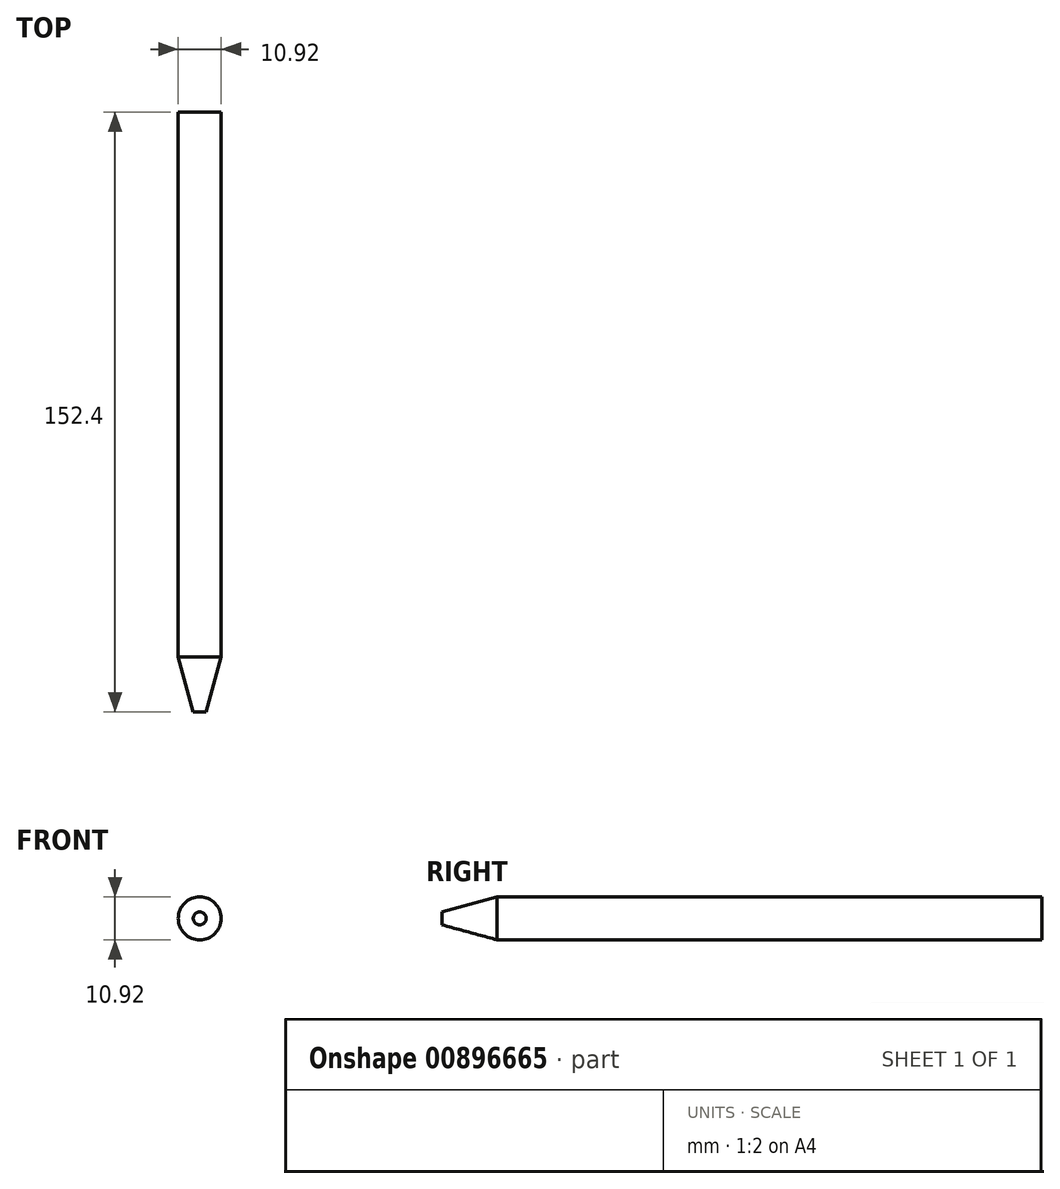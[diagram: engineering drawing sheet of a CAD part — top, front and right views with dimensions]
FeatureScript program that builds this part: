
annotation { "Feature Type Name" : "Feature", "Feature Type Description" : "" }
export const myFeature = defineFeature(function(context is Context, id is Id, definition is map)
    precondition{}
    {
        {
            var Q0;
            Q0=qCreatedBy(makeId("Front.planeOp"),FACE);
            var sketch = newSketch(context, id + "F0", { "sketchPlane" : qUnion([Q0])});
            skCircle(sketch, "E0", {"center": v(0, 0) * mm, "radius": 5.46 * mm});
            skSolve(sketch);
        }
        {
            var Q0;
            Q0 = qSketchRegion(id + "F0", true);
            extrude(context, id + "F1", {"entities" : qUnion([Q0]), "endBound" : BoundingType.SYMMETRIC, "depth" : 152.4 * mm, "offsetDistance" : 25.4 * mm});
        }
        {
            var Q0;
            Q0=makeQuery(id+"F1.opExtrude","CAP_EDGE",EDGE,{"disambiguationData":[OSD([sQuery(id+"F0.wireOp",EDGE,"E0")])],"isStart":false});
            chamfer(context, id + "F2", {"entities" : qUnion([Q0]), "chamferType" : ChamferType.TWO_OFFSETS, "width1" : 3.8 * mm, "oppositeDirection" : false, "width2" : 13.97 * mm, "tangentPropagation" : true});
        }
    });
